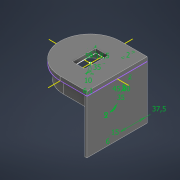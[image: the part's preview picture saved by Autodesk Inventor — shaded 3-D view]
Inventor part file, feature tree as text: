
AUTODESK INVENTOR PART (.ipt)
format: ipt  version: 2022 (Build 260153000, 153)  size: 418,816 bytes
history: native  units: mm
features: extrude x10, sketch x6
ambient origin geometry x8: Origin, YZ Plane, XZ Plane, XY Plane, X Axis, Y Axis, Z Axis, Center Point
bodies: Solid1 (feature_tree)
feature tree (16):
  sketch  "Sketch1"  dims[d0=18.5mm d1=35.0mm]
  extrude  "Extrusion1"  Depth=35.0mm
  extrude  "Extrusion2"  Depth=54.0mm
  extrude  "Extrusion3"  Depth=1.0mm TaperAngle=0.0deg
  extrude  "Extrusion4"  Depth=5.0mm TaperAngle=0.0deg
  extrude  "Extrusion5"  Depth=80.0mm TaperAngle=0.0deg
  extrude  "Extrusion6"  Depth=10.0mm
  extrude  "Extrusion8"  Depth=8.0mm TaperAngle=0.0deg
  sketch  "Sketch5"  dims[d14=3.0mm d15=80.0mm d16=0.0mm]
  extrude  "Extrusion9"  Depth=2.0mm
  extrude  "Extrusion10"  Depth=20.0mm TaperAngle=0.0deg
  extrude  "Extrusion11"  Depth=15.0mm
  sketch  "Sketch2"  dims[d2=67.0mm d3=54.0mm]
  sketch  "Sketch3"  dims[d6=5.0mm d7=0.0mm d8=1.0mm d9=0.0mm]
  sketch  "Sketch4"  dims[d10=0.0mm d11=0.0mm d12=5.0mm d13=0.0mm]
  sketch  "Sketch6"  dims[d18=6.1mm d19=10.0mm d20=8.0mm d21=0.0mm d26=2.0mm d27=20.0mm d28=0.0mm d29=15.0mm d30=6.0mm d31=37.5mm d32=20.0mm d33=0.0mm d34=2.0mm d35=5.0mm d36=0.0mm d37=2.0mm d38=5.0mm d39=35.0mm d40=45.0deg d41=2.0mm d42=5.0mm d43=5.0mm d44=0.0mm]
